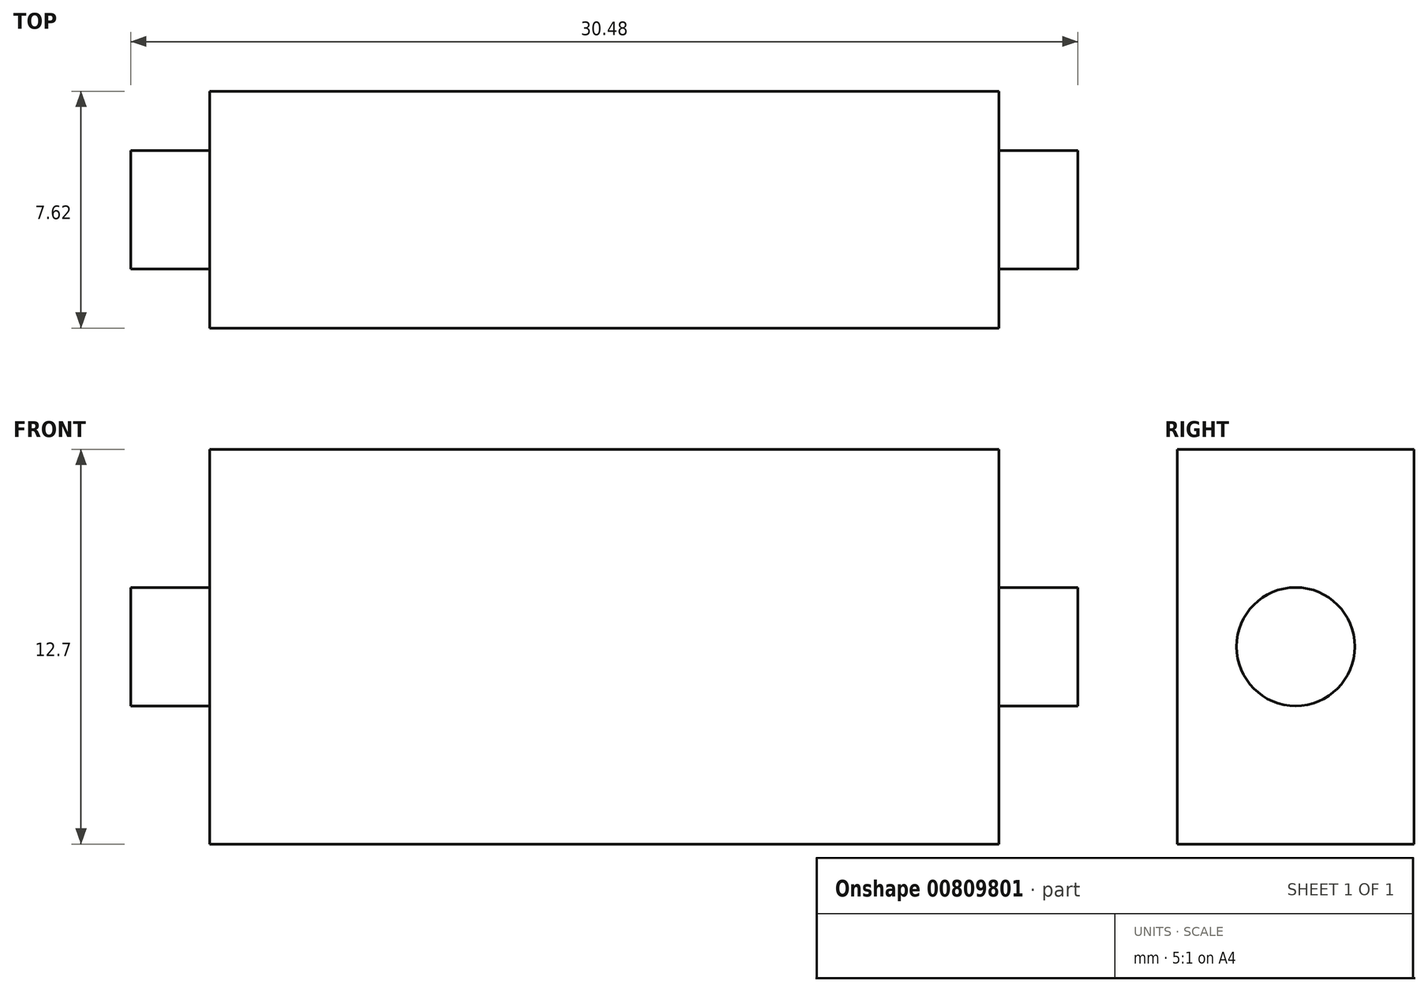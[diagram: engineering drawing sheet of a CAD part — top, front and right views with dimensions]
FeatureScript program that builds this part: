
annotation { "Feature Type Name" : "Feature", "Feature Type Description" : "" }
export const myFeature = defineFeature(function(context is Context, id is Id, definition is map)
    precondition{}
    {
        {
            var Q0;
            Q0=qCreatedBy(makeId("Top.planeOp"),FACE);
            var sketch = newSketch(context, id + "F0", { "sketchPlane" : qUnion([Q0])});
            skLineSegment(sketch, "E0", {"start": v(0, 0) * mm, "end": v(25.4, 0) * mm});
            skLineSegment(sketch, "E1", {"start": v(0, 0) * mm, "end": v(0, -7.62) * mm});
            skLineSegment(sketch, "E2", {"start": v(0, -7.62) * mm, "end": v(25.4, -7.62) * mm});
            skLineSegment(sketch, "E3", {"start": v(25.4, -7.62) * mm, "end": v(25.4, 0) * mm});
            skSolve(sketch);
        }
        {
            var Q0;
            Q0=qSketchRegion(id+"F0",true);
            extrude(context, id + "F1", {"entities" : qUnion([Q0]), "depth" : 12.7 * mm, "offsetDistance" : 25.4 * mm});
        }
        {
            var Q0;
            Q0=makeQuery(id+"F1.opExtrude","SWEPT_FACE",FACE,{"disambiguationData":[OSD([sQuery(id+"F0.wireOp",EDGE,"E3")])]});
            var sketch = newSketch(context, id + "F2", { "sketchPlane" : qUnion([Q0])});
            skLineSegment(sketch, "E4", {"start": v(-7.62, 6.35) * mm, "end": v(0, 6.35) * mm});
            skLineSegment(sketch, "E5", {"start": v(0, 6.35) * mm, "end": v(-3.81, 6.35) * mm});
            skCircle(sketch, "E6", {"center": v(-3.81, 6.35) * mm, "radius": 1.9 * mm});
            skSolve(sketch);
        }
        {
            var Q0;
            Q0=qSketchRegion(id+"F2",true);
            extrude(context, id + "F3", {"entities" : qUnion([Q0]), "operationType" : NewBodyOperationType.ADD, "depth" : 2.54 * mm, "offsetDistance" : 25.4 * mm});
        }
        {
            var Q0;
            Q0=makeQuery(id+"F1.opExtrude","SWEPT_FACE",FACE,{"disambiguationData":[OSD([sQuery(id+"F0.wireOp",EDGE,"E1")])]});
            var sketch = newSketch(context, id + "F4", { "sketchPlane" : qUnion([Q0])});
            skLineSegment(sketch, "E7", {"start": v(0, 6.35) * mm, "end": v(7.62, 6.35) * mm});
            skLineSegment(sketch, "E8", {"start": v(7.62, 6.35) * mm, "end": v(3.81, 6.35) * mm});
            skCircle(sketch, "E9", {"center": v(3.81, 6.35) * mm, "radius": 1.9 * mm});
            skSolve(sketch);
        }
        {
            var Q0;
            Q0=qSketchRegion(id+"F4",true);
            extrude(context, id + "F5", {"entities" : qUnion([Q0]), "operationType" : NewBodyOperationType.ADD, "depth" : 2.54 * mm, "offsetDistance" : 25.4 * mm});
        }
    });
